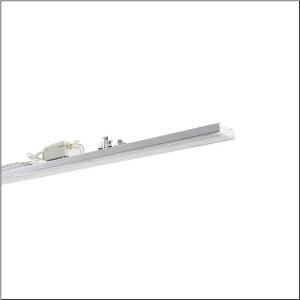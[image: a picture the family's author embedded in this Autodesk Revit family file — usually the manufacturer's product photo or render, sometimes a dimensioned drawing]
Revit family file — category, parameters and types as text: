
# Revit family: licross_11_recessed_ho_51tl1ede465s
name_source: partatom
category: Lighting Fixtures
units: mm (PartAtom-declared; Revit-internal decimal feet)

## family parameters
Cut with Voids When Loaded = No
Host = Face
Light Source = No
Part Type = Normal
Room Calculation Point = No
Round Connector Dimension = Use Diameter
Shared = No

## types (1)
- --- (1 x LED, 6840 lm, 40.2 W, 4000K)
    Apparent Load = 40 VA
    CIE Flux Codes = 85 95 99 100 100
    Color Rendering = 80
    Color Temperature = 4000K
    Default Elevation = 1800 mm
    Description = Licross 11 Recessed HO, luminaire insert, of sheet steel, coil coated, white, length: 750mm, width: 66mm, height: 67mm, LED rated luminous flux: 6.840lm, light colour: 840, SDCM (Standard Deviation of Colour Matching)MacAdam ≤ 2 SDCM (initial), control gear: DALI 2, with plug, 5-pole, with phase selection, mains connection: 220..240V, AC, 50/60Hz, rated input power: 40W, internal wiring halogen-free, primary light control with lens, of plastic, primary optical cover: cover, of PMMA, light emission: direct distribution, primary light characteristic: symmetric, protection rating (complete): IP40, insulation class (complete): insulation class I (protective earthing), certification: CE, ENEC, VDE, UKCA, protection symbol: D if used in an environment without relevant dust loads with corresponding accessories, impact resistance: IK06, permissible ambient temperature for indoor applications: -25..+30°C, corresponds to IFS (International Featured Standards) requirements for safety and quality in the food industry, reducing of maximum allowable ambient temperature of 5°C with ceiling mounting, LABS conformity tested according to VDMA 24364:2018-05, The light source and the operating device comply with the requirements of the Ecodesign Regulation (EU) 2019/2020 and are replaceable in accordance with this regulation, packaging unit: 1 piece
    Height = 58 mm
    Lamp = 1 x LED
    Lamp Light Flux = 6840 lm
    Lamp Power = 40.2 W
    Lamp count = 1
    Length = 750 mm
    Luminous efficacy = 170 lm/W
    Manufacturer = Siteco
    ModVariant = No
    Model = 51TL1EDE465S
    Mounting Place = Ceiling
    Mounting Type = Pendant
    Number of Poles = 1
    OnlyDefault = Yes
    Power Factor = 1
    Product Name = Licross 11 Recessed HO
    Product group = luminaire insert | ceiling pendant
    ProductGroupID = 901
    Protection Class = Protection class I
    Protection Degree = IP 40
    RLX_Detail_Level = 1
    RLX_Emergency_Light_Flux = 0 lm
    RLX_Emergency_Type = 0
    RLX_Emergency_Type_DB = No
    RlxData = <blob elided: 29569 chars, md5=ca3bc169>
    Socket = socket
    Standby Power = 0 W
    System Light Flux = 6840 lm
    System Power = 40 W
    Type Comments = factory setting: luminous flux: 100 % | dim-lin: 254 | 522 mA
    Type Image = l_1296930.jpg
    URL = http://relux.com
    VarID = @adj_100995
    Voltage = 0 V
    Weight = 0.00 kg
    Width = 66 mm

## geometry (parser evidence)
native form markers: Blend x4, Sweep x8
no freeform markers — native parametric forms only
